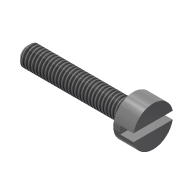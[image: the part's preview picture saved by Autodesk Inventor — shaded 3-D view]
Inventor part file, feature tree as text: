
AUTODESK INVENTOR PART (.ipt)
format: ipt  version: 2015 SP1 (Build 190203100, 203)  size: 105,472 bytes
history: native  units: mm
features: extrude x3, sketch x2, chamfer x1, thread x1, projected_geometry x1
ambient origin geometry x8: Origin, YZ Plane, XZ Plane, XY Plane, X Axis, Y Axis, Z Axis, Center Point
bodies: Solid1 (feature_tree)
feature tree (8):
  sketch  "Sketch1"  dims[d0=3.0mm d1=6.0mm]
  extrude  "Extrusion1"  Depth=3.0mm
  extrude  "Extrusion2"  Depth=3.0mm TaperAngle=0.0deg
  extrude  "Extrusion3"  Depth=2.0mm TaperAngle=0.0deg
  chamfer  "Chamfer1"  Distance=2.0mm Angle=45.0deg
  thread  "Thread2"  [1 undecoded]
  sketch  "Sketch2"  dims[d2=16.0mm d3=0.0mm d4=3.0mm d5=0.0mm d6=2.0mm d7=0.0mm d10=0.5mm d11=2.0mm d12=45.0deg d13=5.0mm d14=0.0mm]
  projected_geometry  "Projected Loop1"
note: 1 required parameter value undecoded (feature->parameter linkage not recoverable at this tier; creation-order binding heuristic only, values carry confidence <= 0.55)
